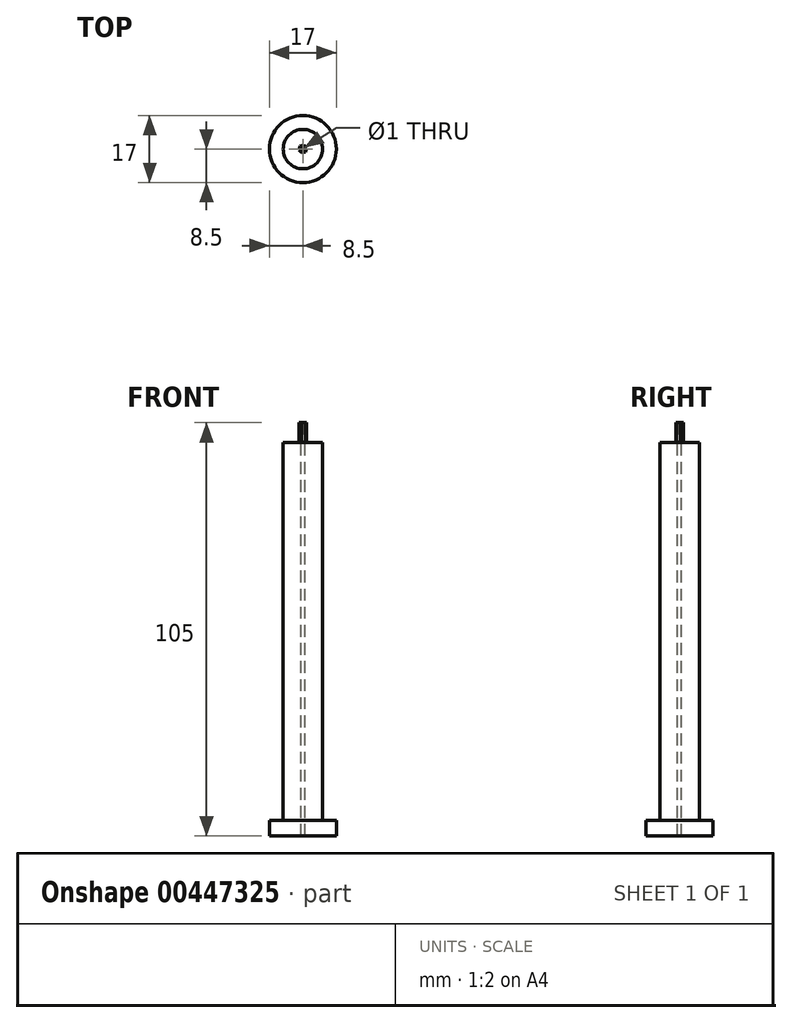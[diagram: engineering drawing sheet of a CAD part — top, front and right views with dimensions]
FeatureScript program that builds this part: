
annotation { "Feature Type Name" : "Feature", "Feature Type Description" : "" }
export const myFeature = defineFeature(function(context is Context, id is Id, definition is map)
    precondition{}
    {
        {
            var Q0;
            Q0=qCreatedBy(makeId("Top.planeOp"),FACE);
            var sketch = newSketch(context, id + "F0", { "sketchPlane" : qUnion([Q0])});
            skCircle(sketch, "E0", {"center": v(0, 0) * mm, "radius": 8.5 * mm});
            skSolve(sketch);
        }
        {
            var Q0;
            Q0=qSketchRegion(id+"F0",true);
            extrude(context, id + "F1", {"entities" : qUnion([Q0]), "depth" : 4 * mm});
        }
        {
            var Q0;
            Q0=qCreatedBy(makeId("Top.planeOp"),FACE);
            var sketch = newSketch(context, id + "F2", { "sketchPlane" : qUnion([Q0])});
            skCircle(sketch, "E1", {"center": v(0, 0) * mm, "radius": 5 * mm});
            skSolve(sketch);
        }
        {
            var Q0;
            Q0=qSketchRegion(id+"F2",true);
            extrude(context, id + "F3", {"entities" : qUnion([Q0]), "operationType" : NewBodyOperationType.ADD, "depth" : 100 * mm});
        }
        {
            var Q0;
            Q0=makeQuery(id+"F3.opExtrude","CAP_FACE",FACE,{"disambiguationData":[OSD([sQuery(id+"F2.wireOp",EDGE,"E1")])],"isStart":false});
            var sketch = newSketch(context, id + "F4", { "sketchPlane" : qUnion([Q0])});
            skCircle(sketch, "E2.cCircle", {"center": v(0, 0) * mm, "radius": 0.87 * mm, "construction": true});
            skLineSegment(sketch, "E2.0", {"start": v(0.98, 0.22) * mm, "end": v(0.67, -0.74) * mm});
            skLineSegment(sketch, "E2.1", {"start": v(0.67, -0.74) * mm, "end": v(-0.3, -0.95) * mm});
            skLineSegment(sketch, "E2.2", {"start": v(-0.3, -0.95) * mm, "end": v(-0.98, -0.22) * mm});
            skLineSegment(sketch, "E2.3", {"start": v(-0.98, -0.22) * mm, "end": v(-0.67, 0.74) * mm});
            skLineSegment(sketch, "E2.4", {"start": v(-0.67, 0.74) * mm, "end": v(0.3, 0.95) * mm});
            skLineSegment(sketch, "E2.5", {"start": v(0.3, 0.95) * mm, "end": v(0.98, 0.22) * mm});
            skPoint(sketch, "E2.0.midPoint", {"position": v(0.83, -0.26) * mm});
            skSolve(sketch);
        }
        {
            var Q0;
            Q0=makeQuery(id+"F4.imprint","IMPRINT",FACE,{"disambiguationData":[TD([[makeQuery(id+"F4.imprint","IMPRINT",EDGE,{"derivedFrom":sQuery(id+"F4.wireOp",EDGE,"E2.0")}),-1.0]])]});
            extrude(context, id + "F5", {"entities" : qUnion([Q0]), "operationType" : NewBodyOperationType.ADD, "depth" : 5 * mm});
        }
        {
            var Q0;
            Q0=makeQuery(id+"F5.opExtrude","CAP_FACE",FACE,{"disambiguationData":[OSD([sQuery(id+"F4.wireOp",EDGE,"E2.0"),sQuery(id+"F4.wireOp",EDGE,"E2.1"),sQuery(id+"F4.wireOp",EDGE,"E2.2"),sQuery(id+"F4.wireOp",EDGE,"E2.3"),sQuery(id+"F4.wireOp",EDGE,"E2.4"),sQuery(id+"F4.wireOp",EDGE,"E2.5")])],"isStart":false});
            var sketch = newSketch(context, id + "F6", { "sketchPlane" : qUnion([Q0])});
            skCircle(sketch, "E3", {"center": v(0, 0) * mm, "radius": 0.5 * mm});
            skSolve(sketch);
        }
        {
            var Q0;
            Q0=makeQuery(id+"F6.imprint","IMPRINT",FACE,{"disambiguationData":[TD([[makeQuery(id+"F6.imprint","IMPRINT",EDGE,{"derivedFrom":sQuery(id+"F6.wireOp",EDGE,"E3")}),1.0]])]});
            extrude(context, id + "F7", {"entities" : qUnion([Q0]), "operationType" : NewBodyOperationType.REMOVE, "oppositeDirection" : true, "depth" : 115.3 * mm});
        }
    });
